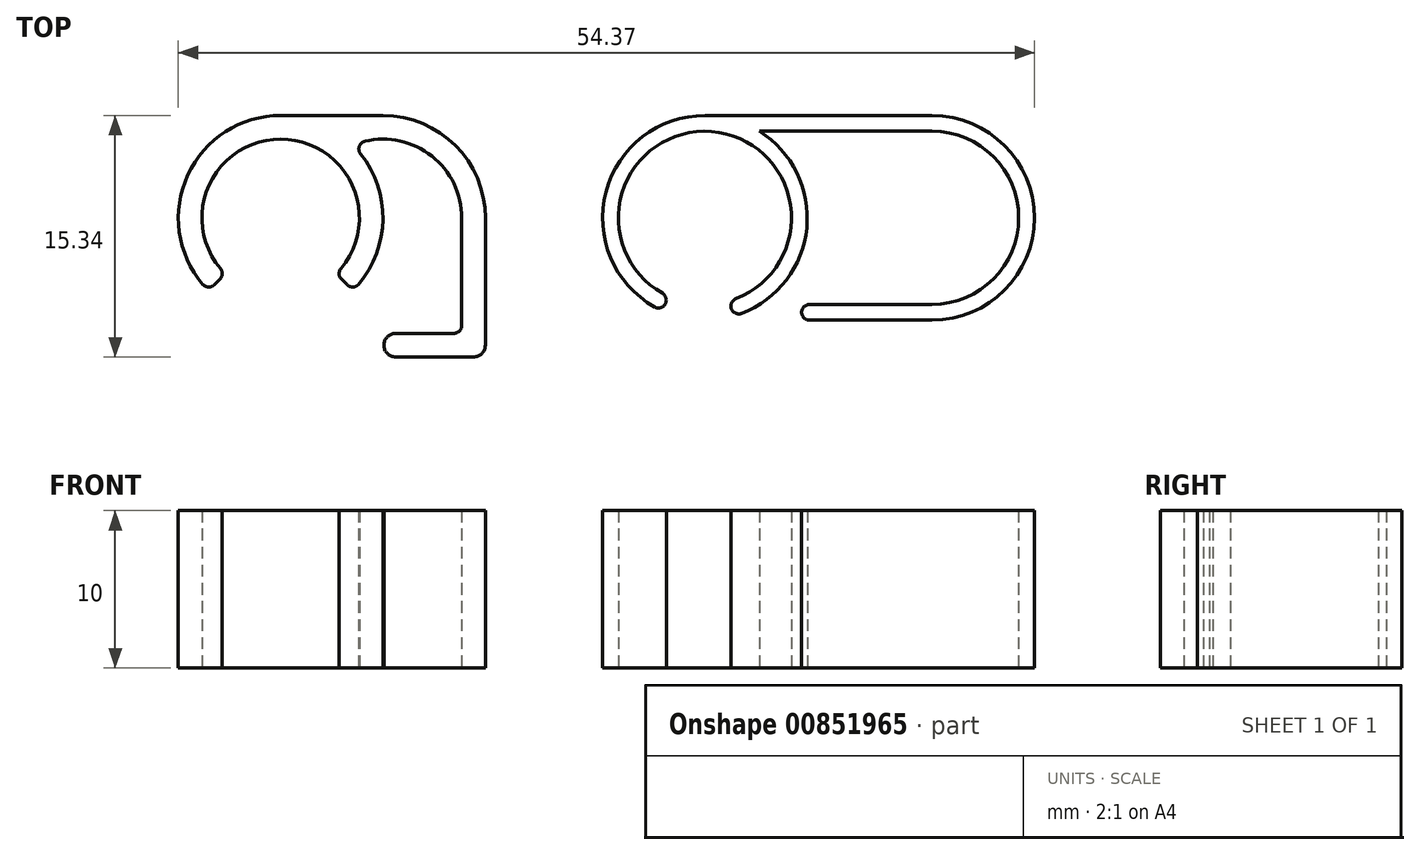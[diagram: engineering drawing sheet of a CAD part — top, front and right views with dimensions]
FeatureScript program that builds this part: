
annotation { "Feature Type Name" : "Feature", "Feature Type Description" : "" }
export const myFeature = defineFeature(function(context is Context, id is Id, definition is map)
    precondition{}
    {
        {
            var Q0;
            Q0=qCreatedBy(makeId("Top.planeOp"),FACE);
            var sketch = newSketch(context, id + "F0", { "sketchPlane" : qUnion([Q0])});
            skArc(sketch, "E0", {"start": v(3.83, -3.22) * mm, "mid": v(0, 5) * mm, "end": v(-3.83, -3.22) * mm});
            skArc(sketch, "E1", {"start": v(4.95, -4.22) * mm, "mid": v(6.5, -0.1) * mm, "end": v(5.07, 4.07) * mm});
            skLineSegment(sketch, "E2", {"start": v(0, 0) * mm, "end": v(6.5, 0) * mm, "construction": true});
            skLineSegment(sketch, "E3", {"start": v(0, 6.5) * mm, "end": v(6.5, 6.5) * mm});
            skArc(sketch, "E4.trimOffspring", {"start": v(0, 6.5) * mm, "mid": v(-5.9, 2.72) * mm, "end": v(-4.95, -4.22) * mm});
            skLineSegment(sketch, "E5", {"start": v(3.86, -3.89) * mm, "end": v(4.21, -4.25) * mm});
            skLineSegment(sketch, "E6", {"start": v(-3.86, -3.89) * mm, "end": v(-4.21, -4.25) * mm});
            skLineSegment(sketch, "E7", {"start": v(6.5, 0) * mm, "end": v(11.5, 0) * mm, "construction": true});
            skArc(sketch, "E8", {"start": v(13, 0) * mm, "mid": v(11.1, 4.6) * mm, "end": v(6.5, 6.5) * mm});
            skLineSegment(sketch, "E9", {"start": v(11.5, 0) * mm, "end": v(13, 0) * mm, "construction": true});
            skArc(sketch, "E10", {"start": v(11.5, 0) * mm, "mid": v(9.6, 3.92) * mm, "end": v(5.35, 4.87) * mm});
            skArc(sketch, "E11.0.endCap", {"start": v(13, -8.09) * mm, "mid": v(12.78, -8.62) * mm, "end": v(12.25, -8.84) * mm});
            skLineSegment(sketch, "E11.0.left", {"start": v(13, 0) * mm, "end": v(13, -8.09) * mm});
            skLineSegment(sketch, "E11.0.right", {"start": v(11.5, 0) * mm, "end": v(11.5, -6.84) * mm});
            skArc(sketch, "E12.0.endCap", {"start": v(7.3, -8.84) * mm, "mid": v(6.55, -8.09) * mm, "end": v(7.3, -7.34) * mm});
            skLineSegment(sketch, "E12.0.left", {"start": v(12.25, -8.84) * mm, "end": v(7.3, -8.84) * mm});
            skLineSegment(sketch, "E12.0.right", {"start": v(11, -7.34) * mm, "end": v(7.3, -7.34) * mm});
            skArc(sketch, "E13.filletArc", {"start": v(11, -7.34) * mm, "mid": v(11.35, -7.19) * mm, "end": v(11.5, -6.84) * mm});
            skPoint(sketch, "E11.0.startCap.center.orphan", {"position": v(12.25, 0) * mm});
            skPoint(sketch, "E14.visualSharp", {"position": v(-3.52, -3.55) * mm});
            skArc(sketch, "E14.filletArc", {"start": v(-3.86, -3.89) * mm, "mid": v(-3.71, -3.56) * mm, "end": v(-3.83, -3.22) * mm});
            skPoint(sketch, "E15.visualSharp", {"position": v(-4.58, -4.62) * mm});
            skArc(sketch, "E15.filletArc", {"start": v(-4.95, -4.22) * mm, "mid": v(-4.58, -4.4) * mm, "end": v(-4.21, -4.25) * mm});
            skPoint(sketch, "E16.visualSharp", {"position": v(3.52, -3.55) * mm});
            skArc(sketch, "E16.filletArc", {"start": v(3.83, -3.22) * mm, "mid": v(3.71, -3.56) * mm, "end": v(3.86, -3.89) * mm});
            skPoint(sketch, "E17.visualSharp", {"position": v(4.58, -4.62) * mm});
            skArc(sketch, "E17.filletArc", {"start": v(4.21, -4.25) * mm, "mid": v(4.58, -4.4) * mm, "end": v(4.95, -4.22) * mm});
            skPoint(sketch, "E18.visualSharp", {"position": v(4.58, 4.62) * mm});
            skArc(sketch, "E18.filletArc", {"start": v(5.35, 4.87) * mm, "mid": v(4.99, 4.54) * mm, "end": v(5.07, 4.07) * mm});
            skArc(sketch, "E19", {"start": v(28.92, -5.13) * mm, "mid": v(27.35, 5.49) * mm, "end": v(24.24, -4.79) * mm});
            skLineSegment(sketch, "E20", {"start": v(30.4, 5.5) * mm, "end": v(41.37, 5.5) * mm});
            skArc(sketch, "E21", {"start": v(41.37, 5.5) * mm, "mid": v(46.87, 0) * mm, "end": v(41.37, -5.5) * mm});
            skLineSegment(sketch, "E22", {"start": v(41.37, 5.5) * mm, "end": v(41.37, -5.5) * mm, "construction": true});
            skLineSegment(sketch, "E23", {"start": v(41.37, -5.5) * mm, "end": v(33.59, -5.5) * mm});
            skLineSegment(sketch, "E24", {"start": v(26.94, 0) * mm, "end": v(28.92, -5.13) * mm, "construction": true});
            skLineSegment(sketch, "E25", {"start": v(26.94, 0) * mm, "end": v(24.24, -4.79) * mm, "construction": true});
            skArc(sketch, "E26", {"start": v(29.28, -6.07) * mm, "mid": v(33.41, -0.63) * mm, "end": v(30.4, 5.5) * mm});
            skArc(sketch, "E27", {"start": v(41.37, -6.5) * mm, "mid": v(47.87, 0) * mm, "end": v(41.37, 6.5) * mm});
            skLineSegment(sketch, "E28", {"start": v(26.94, 6.5) * mm, "end": v(41.37, 6.5) * mm});
            skLineSegment(sketch, "E29", {"start": v(28.92, -5.13) * mm, "end": v(29.28, -6.07) * mm, "construction": true});
            skLineSegment(sketch, "E30", {"start": v(24.24, -4.79) * mm, "end": v(23.74, -5.66) * mm, "construction": true});
            skArc(sketch, "E31.trimOffspring", {"start": v(26.94, 6.5) * mm, "mid": v(20.66, 1.65) * mm, "end": v(23.74, -5.66) * mm});
            skLineSegment(sketch, "E32", {"start": v(41.37, -6.5) * mm, "end": v(33.59, -6.5) * mm});
            skArc(sketch, "E33", {"start": v(33.59, -5.5) * mm, "mid": v(33.09, -6) * mm, "end": v(33.59, -6.5) * mm});
            skArc(sketch, "E34", {"start": v(29.28, -6.07) * mm, "mid": v(28.63, -5.78) * mm, "end": v(28.92, -5.13) * mm});
            skArc(sketch, "E35", {"start": v(24.24, -4.79) * mm, "mid": v(24.43, -5.47) * mm, "end": v(23.74, -5.66) * mm});
            skSolve(sketch);
        }
        {
            var Q0;
            Q0=makeQuery(id+"F0.imprint","IMPRINT",FACE,{"disambiguationData":[TD([[makeQuery(id+"F0.imprint","IMPRINT",EDGE,{"derivedFrom":sQuery(id+"F0.wireOp",EDGE,"E0")}),-1.0]])]});
            var Q1;
            Q1=makeQuery(id+"F0.imprint","IMPRINT",FACE,{"disambiguationData":[TD([[makeQuery(id+"F0.imprint","IMPRINT",EDGE,{"derivedFrom":sQuery(id+"F0.wireOp",EDGE,"E19")}),-1.0]])]});
            extrude(context, id + "F1", {"entities" : qUnion([Q0, Q1]), "depth" : 10 * mm, "offsetDistance" : 25 * mm});
        }
    });
